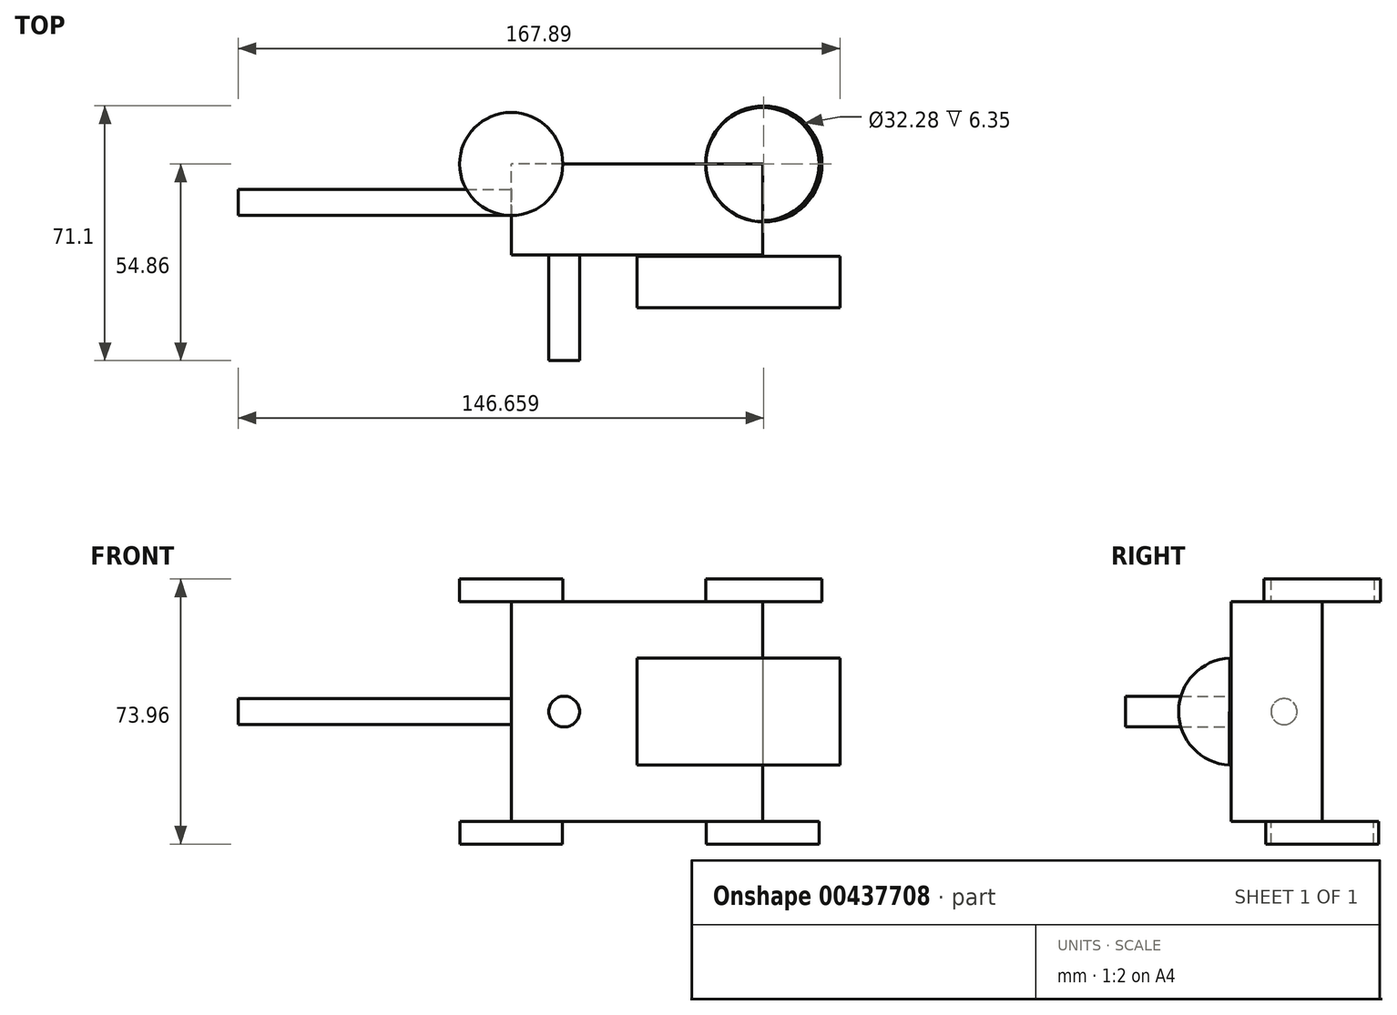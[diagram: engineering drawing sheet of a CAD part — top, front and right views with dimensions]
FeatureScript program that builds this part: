
annotation { "Feature Type Name" : "Feature", "Feature Type Description" : "" }
export const myFeature = defineFeature(function(context is Context, id is Id, definition is map)
    precondition{}
    {
        {
            var Q0;
            Q0=qCreatedBy(makeId("Front.planeOp"),FACE);
            var sketch = newSketch(context, id + "F0", { "sketchPlane" : qUnion([Q0])});
            skLineSegment(sketch, "E0.bottom", {"start": v(35.05, 30.63) * mm, "end": v(-35.05, 30.63) * mm});
            skLineSegment(sketch, "E0.top", {"start": v(35.05, -30.63) * mm, "end": v(-35.05, -30.63) * mm});
            skLineSegment(sketch, "E0.left", {"start": v(35.05, 30.63) * mm, "end": v(35.05, -30.63) * mm});
            skLineSegment(sketch, "E0.right", {"start": v(-35.05, 30.63) * mm, "end": v(-35.05, -30.63) * mm});
            skPoint(sketch, "E0.middle", {"position": v(0, 0) * mm});
            skSolve(sketch);
        }
        {
            var Q0;
            Q0=makeQuery(id+"F0.imprint","IMPRINT",FACE,{"disambiguationData":[TD([[makeQuery(id+"F0.imprint","IMPRINT",EDGE,{"derivedFrom":sQuery(id+"F0.wireOp",EDGE,"E0.bottom")}),1.0]])]});
            extrude(context, id + "F1", {"entities" : qUnion([Q0]), "depth" : 25.4 * mm});
        }
        {
            var Q0;
            Q0=makeQuery(id+"F1.opExtrude","SWEPT_FACE",FACE,{"disambiguationData":[OSD([sQuery(id+"F0.wireOp",EDGE,"E0.top")])]});
            var sketch = newSketch(context, id + "F2", { "sketchPlane" : qUnion([Q0])});
            skCircle(sketch, "E1", {"center": v(-35.05, 0) * mm, "radius": 14.27 * mm});
            skCircle(sketch, "E2", {"center": v(35.05, 0) * mm, "radius": 15.75 * mm});
            skSolve(sketch);
        }
        {
            var Q0;
            Q0 = qSketchRegion(id + "F2", true);
            extrude(context, id + "F3", {"entities" : qUnion([Q0]), "operationType" : NewBodyOperationType.ADD, "depth" : 6.35 * mm});
        }
        {
            var Q0;
            Q0=makeQuery(id+"F1.opExtrude","SWEPT_FACE",FACE,{"disambiguationData":[OSD([sQuery(id+"F0.wireOp",EDGE,"E0.bottom")])]});
            var sketch = newSketch(context, id + "F4", { "sketchPlane" : qUnion([Q0])});
            skCircle(sketch, "E3", {"center": v(35.4, 0) * mm, "radius": 16.24 * mm});
            skCircle(sketch, "E4", {"center": v(-35.17, 0) * mm, "radius": 14.27 * mm});
            skCircle(sketch, "E5", {"center": v(-35.05, 0) * mm, "radius": 14.39 * mm});
            skCircle(sketch, "E6", {"center": v(35.4, 0) * mm, "radius": 16.14 * mm});
            skSolve(sketch);
        }
        {
            var Q0;
            Q0 = qSketchRegion(id + "F4", true);
            extrude(context, id + "F5", {"entities" : qUnion([Q0]), "operationType" : NewBodyOperationType.ADD, "depth" : 6.35 * mm});
        }
        {
            var Q0;
            Q0=makeQuery(id+"F1.opExtrude","SWEPT_FACE",FACE,{"disambiguationData":[OSD([sQuery(id+"F0.wireOp",EDGE,"E0.right")])]});
            var sketch = newSketch(context, id + "F6", { "sketchPlane" : qUnion([Q0])});
            skCircle(sketch, "E7", {"center": v(10.67, 0) * mm, "radius": 3.62 * mm});
            skSolve(sketch);
        }
        {
            var Q0;
            Q0=makeQuery(id+"F6.imprint","IMPRINT",FACE,{"disambiguationData":[TD([[makeQuery(id+"F6.imprint","IMPRINT",EDGE,{"derivedFrom":sQuery(id+"F6.wireOp",EDGE,"E7")}),1.0]])]});
            extrude(context, id + "F7", {"entities" : qUnion([Q0]), "operationType" : NewBodyOperationType.ADD, "depth" : 76.2 * mm});
        }
        {
            var Q0;
            Q0=qCreatedBy(makeId("Right.planeOp"),FACE);
            var sketch = newSketch(context, id + "F8", { "sketchPlane" : qUnion([Q0])});
            skArc(sketch, "E8", {"start": v(-25.76, 14.94) * mm, "mid": v(-40.1, 0.09) * mm, "end": v(-25.93, -14.93) * mm});
            skLineSegment(sketch, "E9", {"start": v(-25.76, 14.94) * mm, "end": v(-25.93, -14.93) * mm});
            skSolve(sketch);
        }
        {
            var Q0;
            Q0=makeQuery(id+"F8.imprint","IMPRINT",FACE,{"disambiguationData":[TD([[makeQuery(id+"F8.imprint","IMPRINT",EDGE,{"derivedFrom":sQuery(id+"F8.wireOp",EDGE,"E8")}),1.0]])]});
            extrude(context, id + "F9", {"entities" : qUnion([Q0]), "depth" : 56.64 * mm});
        }
        {
            var Q0;
            Q0=makeQuery(id+"F1.opExtrude","CAP_FACE",FACE,{"disambiguationData":[OSD([sQuery(id+"F0.wireOp",EDGE,"E0.bottom"),sQuery(id+"F0.wireOp",EDGE,"E0.top"),sQuery(id+"F0.wireOp",EDGE,"E0.left"),sQuery(id+"F0.wireOp",EDGE,"E0.right")])],"isStart":false});
            var sketch = newSketch(context, id + "F10", { "sketchPlane" : qUnion([Q0])});
            skCircle(sketch, "E10", {"center": v(-20.27, 0) * mm, "radius": 4.3 * mm});
            skSolve(sketch);
        }
        {
            var Q0;
            Q0 = qSketchRegion(id + "F10", true);
            extrude(context, id + "F11", {"entities" : qUnion([Q0]), "operationType" : NewBodyOperationType.ADD, "depth" : 29.46 * mm});
        }
    });
